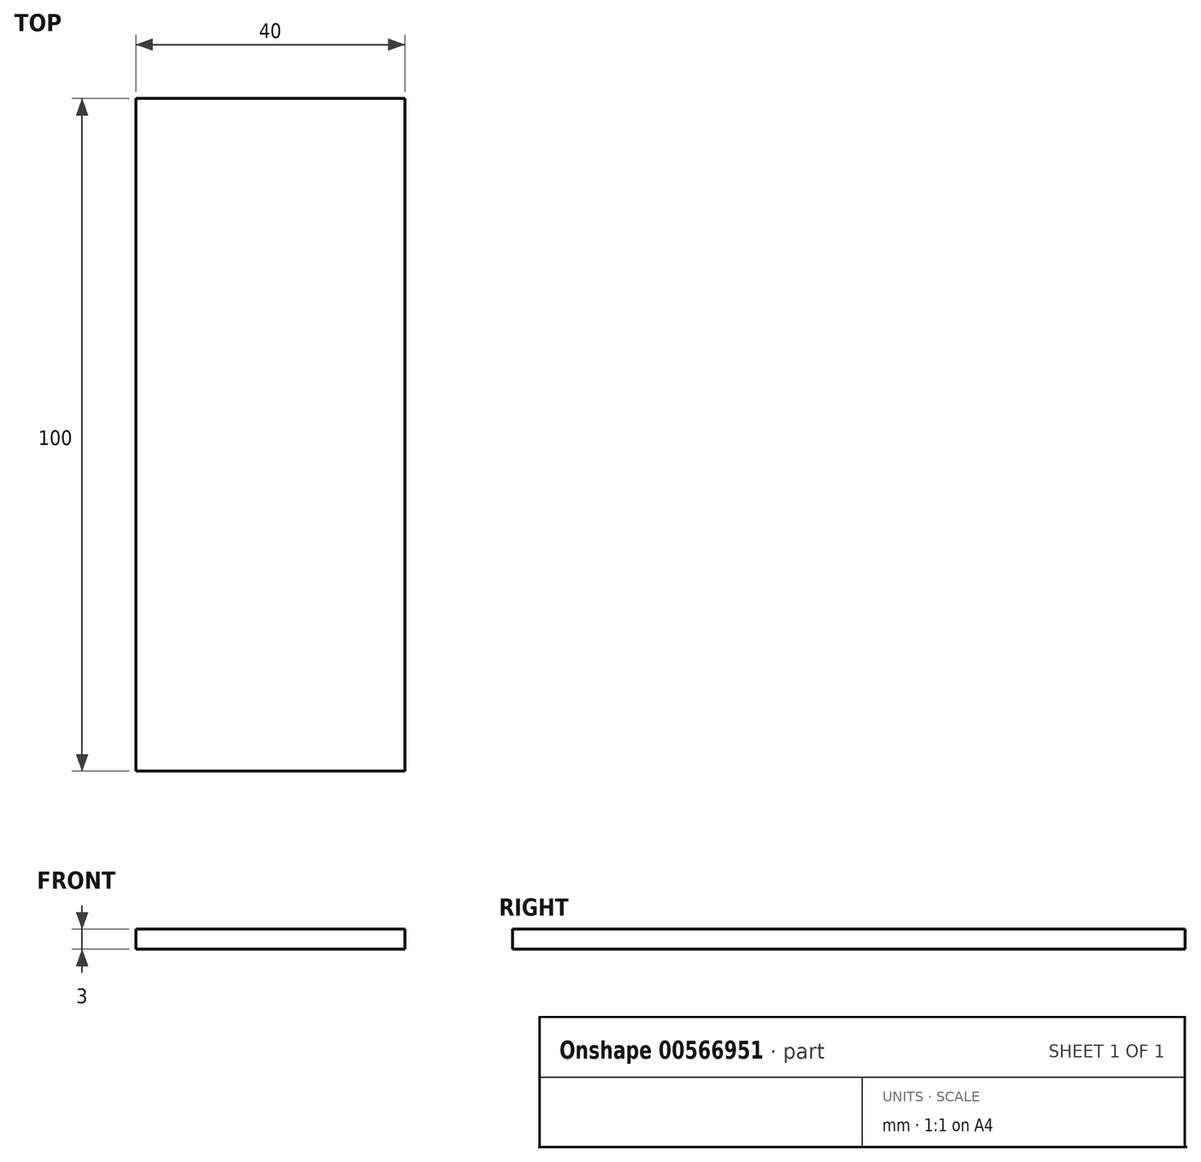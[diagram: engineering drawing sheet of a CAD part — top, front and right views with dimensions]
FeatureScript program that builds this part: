
annotation { "Feature Type Name" : "Feature", "Feature Type Description" : "" }
export const myFeature = defineFeature(function(context is Context, id is Id, definition is map)
    precondition{}
    {
        {
            var Q0;
            Q0=qCreatedBy(makeId("Top.planeOp"),FACE);
            var sketch = newSketch(context, id + "F0", { "sketchPlane" : qUnion([Q0])});
            skLineSegment(sketch, "E0.bottom", {"start": v(0, 100) * mm, "end": v(40, 100) * mm});
            skLineSegment(sketch, "E0.top", {"start": v(0, 0) * mm, "end": v(40, 0) * mm});
            skLineSegment(sketch, "E0.left", {"start": v(0, 100) * mm, "end": v(0, 0) * mm});
            skLineSegment(sketch, "E0.right", {"start": v(40, 100) * mm, "end": v(40, 0) * mm});
            skSolve(sketch);
        }
        {
            var Q0;
            Q0 = qSketchRegion(id + "F0", true);
            extrude(context, id + "F1", {"entities" : qUnion([Q0]), "depth" : 3 * mm, "offsetDistance" : 25 * mm});
        }
    });
